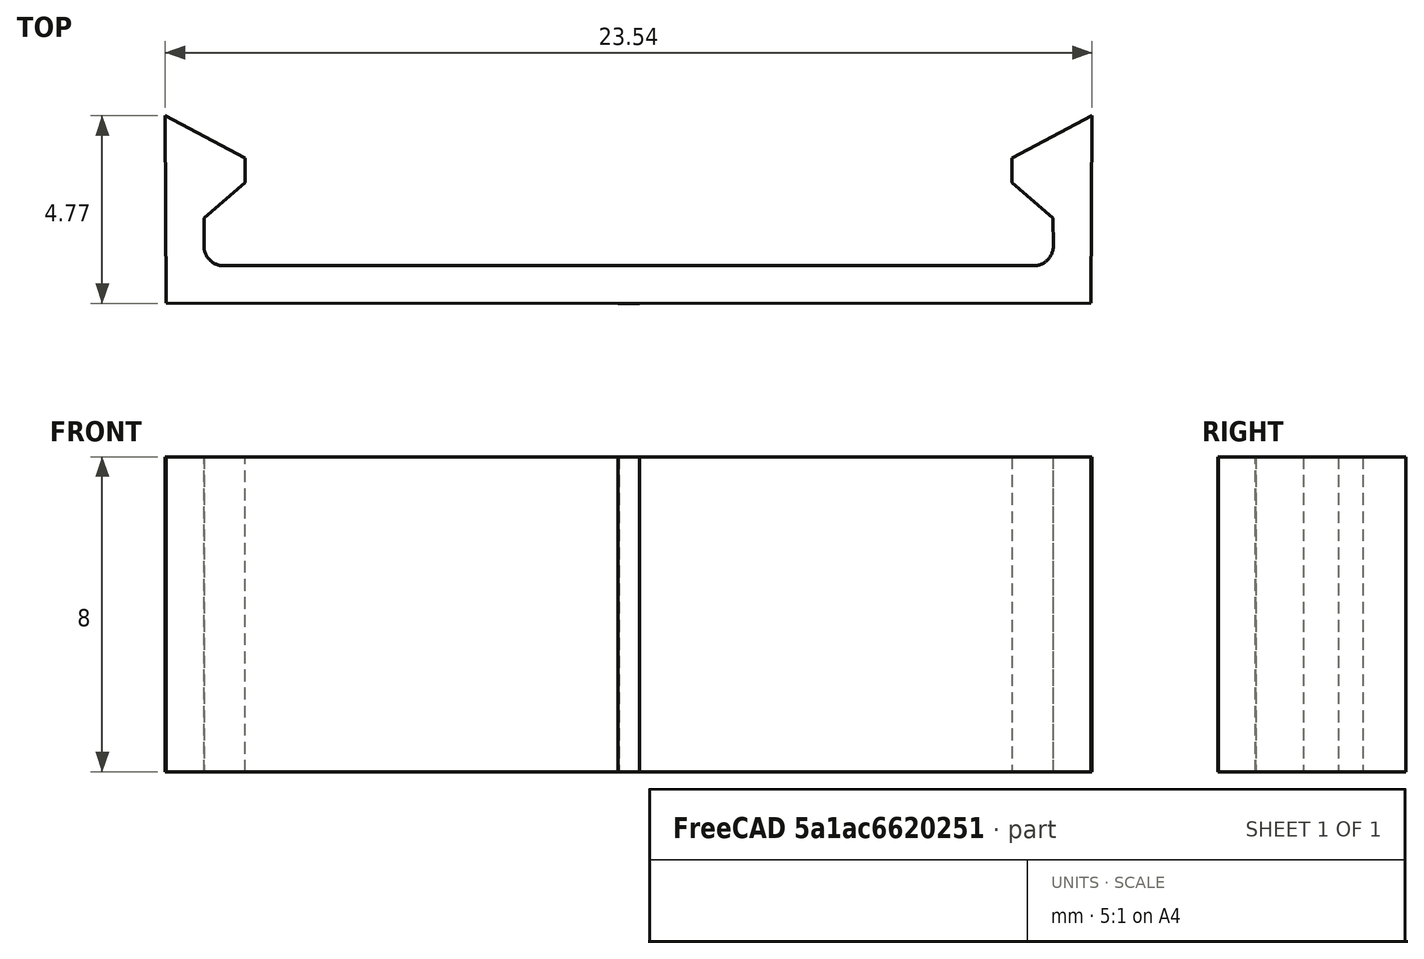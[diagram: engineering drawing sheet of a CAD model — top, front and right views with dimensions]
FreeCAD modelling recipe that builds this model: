
FCSTD DOCUMENT  (FreeCAD 0.18.4R)
Label: 21mmClip
License: All rights reserved
LicenseURL: http://en.wikipedia.org/wiki/All_rights_reserved
objects: Sketcher::SketchObject×2, Part::Extrusion×2, Part::MultiFuse×1, Mesh::Feature×1
note: 5 computed .brp shape members not serialized (recipe doc carries the construction recipe); baked Part::Feature solids carry a one-line shape summary decoded from their .brp

FEATURE [Sketcher::SketchObject] Sketch001
  sketch-geometry (9):
    g0: LineSegment StartX=-20.0003 StartY=-0.953855 StartZ=0 EndX=-7.97838 EndY=-0.972472 EndZ=0
    g1: LineSegment StartX=-20.0199 StartY=3.80263 StartZ=0 EndX=-20.0003 EndY=-0.953855 EndZ=0
    g2: LineSegment StartX=-20.0199 StartY=3.80263 StartZ=0 EndX=-17.9899 EndY=2.71843 EndZ=0
    g3: LineSegment StartX=-17.9899 StartY=2.71843 StartZ=0 EndX=-17.9899 EndY=2.09559 EndZ=0
    g4: LineSegment StartX=-19.031 StartY=1.2011 StartZ=0 EndX=-17.9899 EndY=2.09559 EndZ=0
    g5: LineSegment StartX=-19.031 StartY=1.2011 StartZ=0 EndX=-19.0379 EndY=0.490126 EndZ=0
    g6: LineSegment StartX=-18.5397 StartY=-0.0124554 StartZ=0 EndX=-8.00145 EndY=-0.003612 EndZ=0
    g7: LineSegment StartX=-8.00145 StartY=-0.003612 StartZ=0 EndX=-7.97838 EndY=-0.972472 EndZ=0
    g8: ArcOfCircle CenterX=-18.5401 CenterY=0.485335 CenterZ=0 NormalX=0 NormalY=0 NormalZ=1 AngleXU=0 Radius=0.49779 StartAngle=3.13197 EndAngle=4.71323
  constraints (9):
    c: Coincident(g1,g0)
    c: Coincident(g1,g2)
    c: Coincident(g2,g3)
    c: Coincident(g3,g4)
    c: Coincident(g6,g7)
    c: Coincident(g0,g7)
    c: Tangent(g5,g8) = -1.5708
    c: Tangent(g6,g8) = -1.5708
    c: Coincident(g5,g4)
FEATURE [Part::Extrusion] Extrude001
  Base = -> Sketch001
  Dir = (0,0,1)
  DirMode = 2
  FaceMakerClass = Part::FaceMakerBullseye
  LengthFwd = 8
  LengthRev = 0
  Placement = pos=(-15,0,8) rot=(0,1,0;3.14159rad)
  Solid = true
  Symmetric = false
FEATURE [Sketcher::SketchObject] Sketch002
  sketch-geometry (9):
    g0: LineSegment StartX=-20.0003 StartY=-0.953855 StartZ=0 EndX=-7.97838 EndY=-0.972472 EndZ=0
    g1: LineSegment StartX=-20.0199 StartY=3.80263 StartZ=0 EndX=-20.0003 EndY=-0.953855 EndZ=0
    g2: LineSegment StartX=-20.0199 StartY=3.80263 StartZ=0 EndX=-17.9899 EndY=2.71843 EndZ=0
    g3: LineSegment StartX=-17.9899 StartY=2.71843 StartZ=0 EndX=-17.9899 EndY=2.09559 EndZ=0
    g4: LineSegment StartX=-19.031 StartY=1.2011 StartZ=0 EndX=-17.9899 EndY=2.09559 EndZ=0
    g5: LineSegment StartX=-19.031 StartY=1.2011 StartZ=0 EndX=-19.0379 EndY=0.490126 EndZ=0
    g6: LineSegment StartX=-18.5397 StartY=-0.0124554 StartZ=0 EndX=-8.00145 EndY=-0.003612 EndZ=0
    g7: LineSegment StartX=-8.00145 StartY=-0.003612 StartZ=0 EndX=-7.97838 EndY=-0.972472 EndZ=0
    g8: ArcOfCircle CenterX=-18.5401 CenterY=0.485335 CenterZ=0 NormalX=0 NormalY=0 NormalZ=1 AngleXU=0 Radius=0.49779 StartAngle=3.13197 EndAngle=4.71323
  constraints (9):
    c: Coincident(g1,g0)
    c: Coincident(g1,g2)
    c: Coincident(g2,g3)
    c: Coincident(g3,g4)
    c: Coincident(g6,g7)
    c: Coincident(g0,g7)
    c: Tangent(g5,g8) = -1.5708
    c: Tangent(g6,g8) = -1.5708
    c: Coincident(g5,g4)
FEATURE [Part::Extrusion] Extrude002
  Base = -> Sketch002
  Dir = (0,0,1)
  DirMode = 2
  FaceMakerClass = Part::FaceMakerBullseye
  LengthFwd = 8
  LengthRev = 0
  Placement = pos=(1.5,0,0) rot=(0,1,0;0rad)
  Solid = true
  Symmetric = false
FEATURE [Part::MultiFuse] Fusion
  Shapes = -> [Extrude001,Extrude002]
FEATURE [Mesh::Feature] Mesh  label="Fusion (Meshed)"
